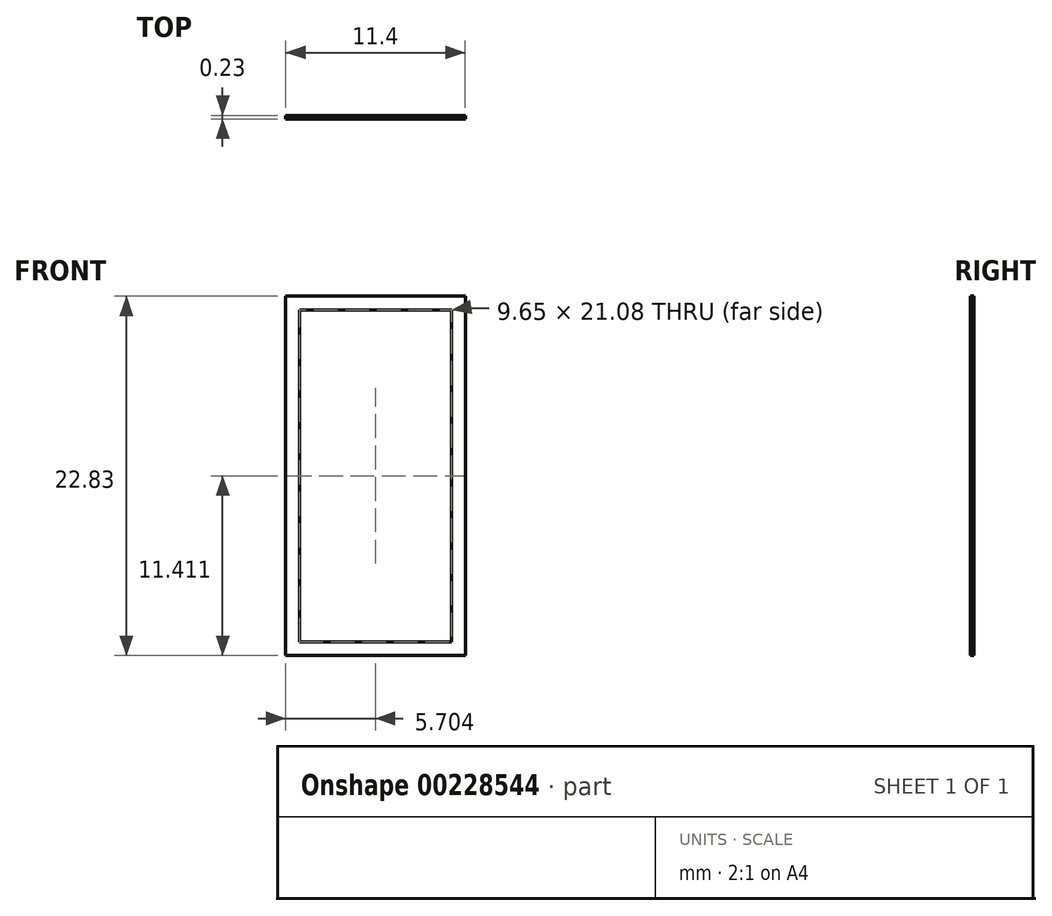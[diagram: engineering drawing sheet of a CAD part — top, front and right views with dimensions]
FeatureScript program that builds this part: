
annotation { "Feature Type Name" : "Feature", "Feature Type Description" : "" }
export const myFeature = defineFeature(function(context is Context, id is Id, definition is map)
    precondition{}
    {
        {
            var Q0;
            Q0=qCreatedBy(makeId("Front.planeOp"),FACE);
            var sketch = newSketch(context, id + "F0", { "sketchPlane" : qUnion([Q0])});
            skLineSegment(sketch, "E0.bottom", {"start": v(0, 0) * mm, "end": v(-9.65, 0) * mm});
            skLineSegment(sketch, "E0.top", {"start": v(0, 21.08) * mm, "end": v(-9.65, 21.08) * mm});
            skLineSegment(sketch, "E0.left", {"start": v(0, 0) * mm, "end": v(0, 21.08) * mm});
            skLineSegment(sketch, "E0.right", {"start": v(-9.65, 0) * mm, "end": v(-9.65, 21.08) * mm});
            skLineSegment(sketch, "E1.bottom", {"start": v(0.87, -0.87) * mm, "end": v(-10.53, -0.87) * mm});
            skLineSegment(sketch, "E1.top", {"start": v(0.87, 21.96) * mm, "end": v(-10.53, 21.96) * mm});
            skLineSegment(sketch, "E1.left", {"start": v(0.87, -0.87) * mm, "end": v(0.87, 21.96) * mm});
            skLineSegment(sketch, "E1.right", {"start": v(-10.53, -0.87) * mm, "end": v(-10.53, 21.96) * mm});
            skSolve(sketch);
        }
        {
            var Q0;
            Q0=makeQuery(id+"F0.imprint","IMPRINT",FACE,{"disambiguationData":[TD([[makeQuery(id+"F0.imprint","IMPRINT",EDGE,{"derivedFrom":sQuery(id+"F0.wireOp",EDGE,"E0.bottom")}),1.0]])]});
            extrude(context, id + "F1", {"entities" : qUnion([Q0]), "depth" : 0.23 * mm});
        }
    });
